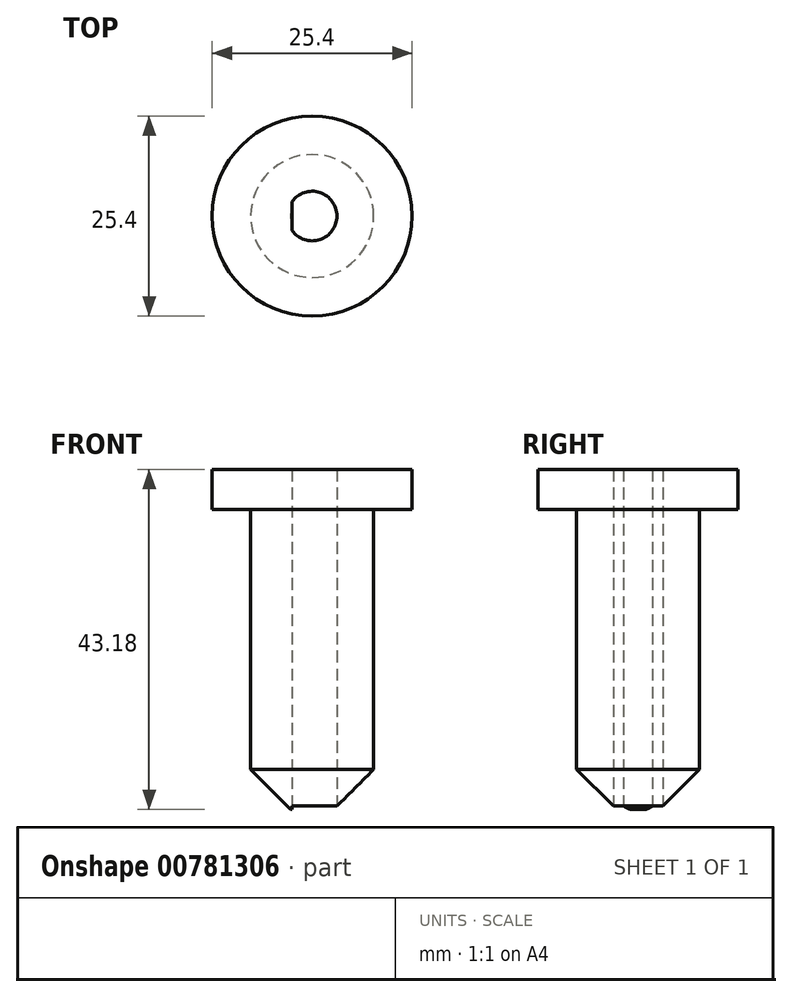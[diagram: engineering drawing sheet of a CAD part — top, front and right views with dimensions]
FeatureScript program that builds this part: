
annotation { "Feature Type Name" : "Feature", "Feature Type Description" : "" }
export const myFeature = defineFeature(function(context is Context, id is Id, definition is map)
    precondition{}
    {
        {
            var Q0;
            Q0=qCreatedBy(makeId("Top.planeOp"),FACE);
            var sketch = newSketch(context, id + "F0", { "sketchPlane" : qUnion([Q0])});
            skArc(sketch, "E0", {"start": v(-2.55, -1.85) * mm, "mid": v(3.15, 0) * mm, "end": v(-2.55, 1.85) * mm});
            skLineSegment(sketch, "E1", {"start": v(-2.55, 1.85) * mm, "end": v(-2.55, -1.85) * mm});
            skLineSegment(sketch, "E2", {"start": v(3.15, 0) * mm, "end": v(-3.15, 0) * mm, "construction": true});
            skSolve(sketch);
        }
        {
            var Q0;
            Q0=qCreatedBy(makeId("Top.planeOp"),FACE);
            var sketch = newSketch(context, id + "F1", { "sketchPlane" : qUnion([Q0])});
            skCircle(sketch, "E3", {"center": v(0, 0) * mm, "radius": 7.81 * mm});
            skSolve(sketch);
        }
        {
            var Q0;
            Q0=makeQuery(id+"F1.imprint","IMPRINT",FACE,{"disambiguationData":[TD([[makeQuery(id+"F1.imprint","IMPRINT",EDGE,{"derivedFrom":sQuery(id+"F1.wireOp",EDGE,"E3")}),1.0]])]});
            extrude(context, id + "F2", {"entities" : qUnion([Q0]), "depth" : 38.1 * mm, "offsetDistance" : 25.4 * mm});
        }
        {
            var Q0;
            Q0=qSketchRegion(id+"F0",true);
            extrude(context, id + "F3", {"entities" : qUnion([Q0]), "operationType" : NewBodyOperationType.REMOVE, "depth" : 50.8 * mm, "offsetDistance" : 25.4 * mm});
        }
        {
            var Q0;
            Q0=makeQuery(id+"F2.opExtrude","CAP_FACE",FACE,{"disambiguationData":[OSD([sQuery(id+"F1.wireOp",EDGE,"E3")])],"isStart":false});
            var sketch = newSketch(context, id + "F4", { "sketchPlane" : qUnion([Q0])});
            skCircle(sketch, "E4", {"center": v(0, 0) * mm, "radius": 12.7 * mm});
            skSolve(sketch);
        }
        {
            var Q0;
            Q0=makeQuery(id+"F4.imprint","IMPRINT",FACE,{"disambiguationData":[TD([[makeQuery(id+"F4.imprint","IMPRINT",EDGE,{"derivedFrom":sQuery(id+"F4.wireOp",EDGE,"E4")}),1.0]])]});
            var Q1;
            {var subQ0=sQuery(id+"F1.wireOp",EDGE,"E3");Q1=makeQuery(id+"F4.imprint","IMPRINT",FACE,{"disambiguationData":[TD([[makeQuery(id+"F4.imprint","IMPRINT",EDGE,{"derivedFrom":makeQuery(id+"F2.opExtrude","CAP_EDGE",EDGE,{"disambiguationData":[OSD([subQ0])],"isStart":false})}),1.0]])]});}
            extrude(context, id + "F5", {"entities" : qUnion([Q0, Q1]), "operationType" : NewBodyOperationType.ADD, "depth" : 5.08 * mm, "offsetDistance" : 25.4 * mm});
        }
        {
            var Q0;
            Q0=makeQuery(id+"F2.opExtrude","CAP_EDGE",EDGE,{"disambiguationData":[OSD([sQuery(id+"F1.wireOp",EDGE,"E3")])],"isStart":true});
            chamfer(context, id + "F6", {"entities" : qUnion([Q0]), "width" : 5.08 * mm, "tangentPropagation" : true});
        }
    });
